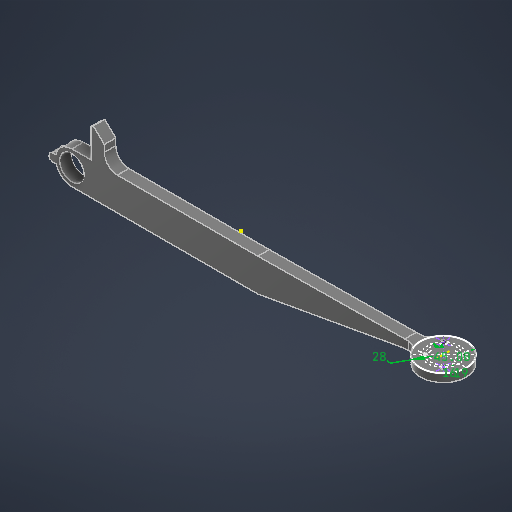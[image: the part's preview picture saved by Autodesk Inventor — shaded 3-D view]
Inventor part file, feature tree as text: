
AUTODESK INVENTOR PART (.ipt)
format: ipt  version: 2025 (Build 290162010, 162A)  size: 293,888 bytes
history: native  units: mm
features: extrude x3, sketch x3, fillet x2, hole x1
ambient origin geometry x8: Origin, YZ Plane, XZ Plane, XY Plane, X Axis, Y Axis, Z Axis, Center Point
bodies: Solid1 (feature_tree)
feature tree (9):
  extrude  "Extrusion1"  Depth=20.0mm
  sketch  "Sketch2"  dims[d2=203.2mm d3=20.0mm]
  extrude  "Extrusion2"  Depth=20.0mm
  hole  "Hole1"  [1 undecoded]
  fillet  "Fillet1"  Radius=28.0mm
  extrude  "Extrusion4"  Depth=2.0mm
  fillet  "Fillet3"  Radius=16.0mm
  sketch  "Sketch1"  dims[d0=20.0mm d1=15.0mm]
  sketch  "Sketch4"  dims[d4=5.0mm d5=7.0mm d6=0.0mm d7=28.0mm d8=19.0mm d9=16.0mm d10=45.0deg d11=5.0mm d12=0.0mm d13=3.0mm d14=6.0mm d15=4.0mm d16=2.0mm d17=90.0deg d18=4.0mm d19=0.0mm d23=6.0mm d37=10.0mm d38=0.0mm d39=8.0mm d42=8.0mm d43=2.0mm d41=0.5mm d44=0.872665mm]
note: 1 required parameter value undecoded (feature->parameter linkage not recoverable at this tier; creation-order binding heuristic only, values carry confidence <= 0.55)
